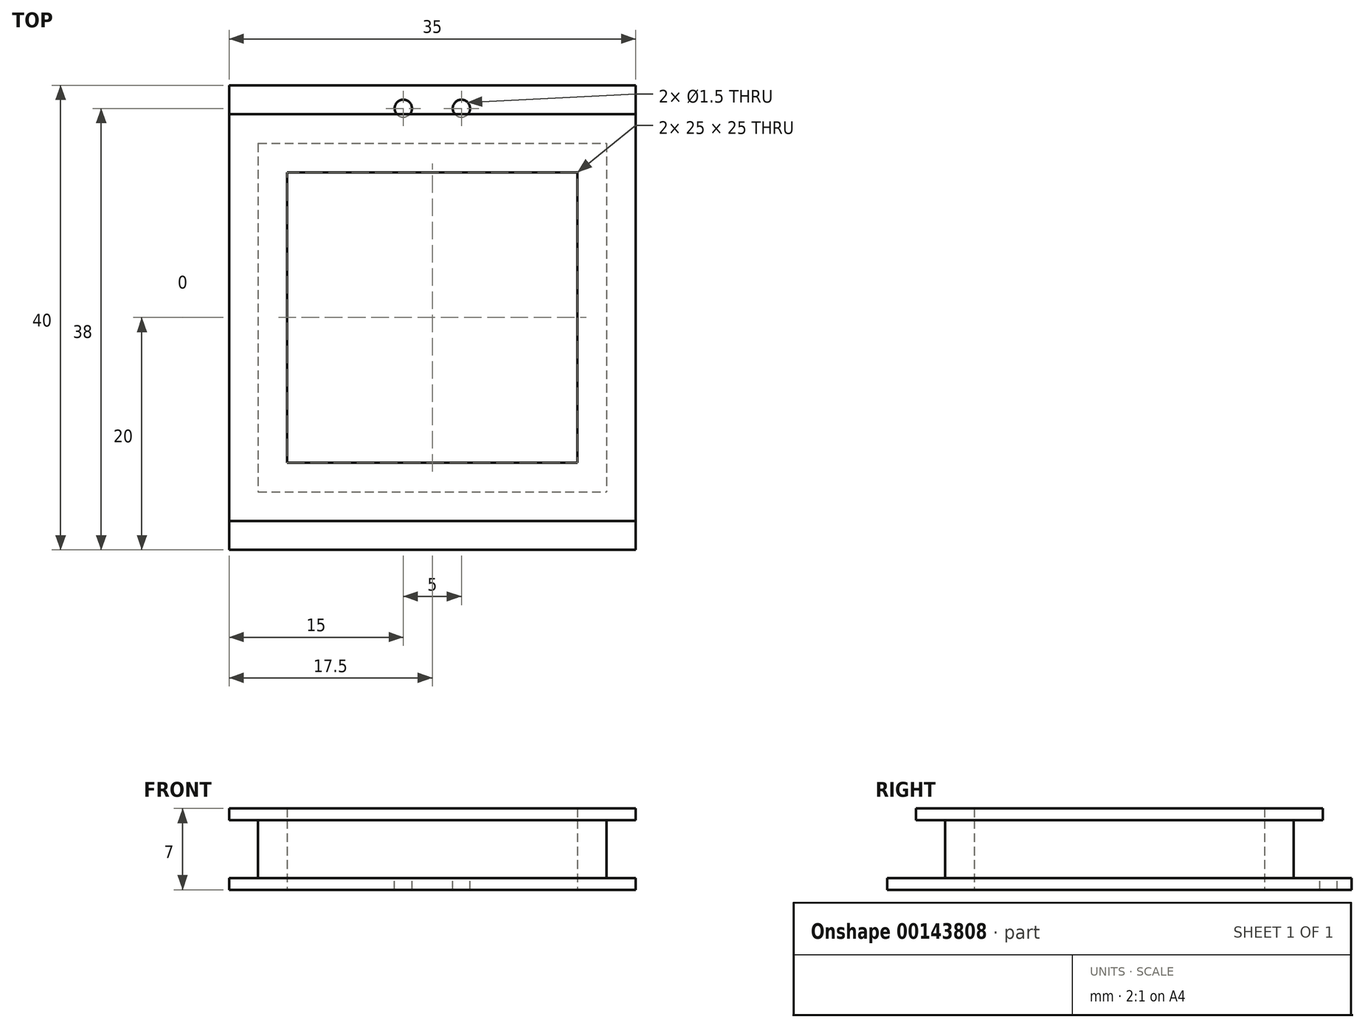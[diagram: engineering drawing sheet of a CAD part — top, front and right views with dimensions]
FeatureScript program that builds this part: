
annotation { "Feature Type Name" : "Feature", "Feature Type Description" : "" }
export const myFeature = defineFeature(function(context is Context, id is Id, definition is map)
    precondition{}
    {
        {
            var Q0;
            Q0=qCreatedBy(makeId("Top.planeOp"),FACE);
            var sketch = newSketch(context, id + "F0", { "sketchPlane" : qUnion([Q0])});
            skLineSegment(sketch, "E0.bottom", {"start": v(-15, 15) * mm, "end": v(15, 15) * mm});
            skLineSegment(sketch, "E0.top", {"start": v(-15, -15) * mm, "end": v(15, -15) * mm});
            skLineSegment(sketch, "E0.left", {"start": v(-15, 15) * mm, "end": v(-15, -15) * mm});
            skLineSegment(sketch, "E0.right", {"start": v(15, 15) * mm, "end": v(15, -15) * mm});
            skPoint(sketch, "E0.middle", {"position": v(0, 0) * mm});
            skLineSegment(sketch, "E1.bottom", {"start": v(-12.5, 12.5) * mm, "end": v(12.5, 12.5) * mm});
            skLineSegment(sketch, "E1.top", {"start": v(-12.5, -12.5) * mm, "end": v(12.5, -12.5) * mm});
            skLineSegment(sketch, "E1.left", {"start": v(-12.5, 12.5) * mm, "end": v(-12.5, -12.5) * mm});
            skLineSegment(sketch, "E1.right", {"start": v(12.5, 12.5) * mm, "end": v(12.5, -12.5) * mm});
            skSolve(sketch);
        }
        {
            var Q0;
            Q0=makeQuery(id+"F0.imprint","IMPRINT",FACE,{"disambiguationData":[TD([[makeQuery(id+"F0.imprint","IMPRINT",EDGE,{"derivedFrom":sQuery(id+"F0.wireOp",EDGE,"E0.bottom")}),-1.0]])]});
            extrude(context, id + "F1", {"entities" : qUnion([Q0]), "depth" : 5 * mm});
        }
        {
            var Q0;
            Q0=makeQuery(id+"F1.opExtrude","CAP_FACE",FACE,{"disambiguationData":[OSD([sQuery(id+"F0.wireOp",EDGE,"E0.bottom"),sQuery(id+"F0.wireOp",EDGE,"E0.top"),sQuery(id+"F0.wireOp",EDGE,"E0.left"),sQuery(id+"F0.wireOp",EDGE,"E0.right"),sQuery(id+"F0.wireOp",EDGE,"E1.bottom"),sQuery(id+"F0.wireOp",EDGE,"E1.top"),sQuery(id+"F0.wireOp",EDGE,"E1.left"),sQuery(id+"F0.wireOp",EDGE,"E1.right")])],"isStart":false});
            var sketch = newSketch(context, id + "F2", { "sketchPlane" : qUnion([Q0])});
            skLineSegment(sketch, "E2.bottom", {"start": v(-17.5, 17.5) * mm, "end": v(17.5, 17.5) * mm});
            skLineSegment(sketch, "E2.top", {"start": v(-17.5, -17.5) * mm, "end": v(17.5, -17.5) * mm});
            skLineSegment(sketch, "E2.left", {"start": v(-17.5, 17.5) * mm, "end": v(-17.5, -17.5) * mm});
            skLineSegment(sketch, "E2.right", {"start": v(17.5, 17.5) * mm, "end": v(17.5, -17.5) * mm});
            skPoint(sketch, "E2.middle", {"position": v(0, 0) * mm});
            skSolve(sketch);
        }
        {
            var Q0;
            Q0=makeQuery(id+"F2.imprint","IMPRINT",FACE,{"disambiguationData":[TD([[makeQuery(id+"F2.imprint","IMPRINT",EDGE,{"derivedFrom":sQuery(id+"F2.wireOp",EDGE,"E2.bottom")}),-1.0]])]});
            var Q1;
            Q1=makeQuery(id+"F2.imprint","IMPRINT",FACE,{"disambiguationData":[TD([[makeQuery(id+"F2.imprint","IMPRINT",EDGE,{"derivedFrom":makeQuery(id+"F1.opExtrude","CAP_EDGE",EDGE,{"disambiguationData":[OSD([sQuery(id+"F0.wireOp",EDGE,"E0.bottom")])],"isStart":false})}),-1.0]])]});
            extrude(context, id + "F3", {"entities" : qUnion([Q0, Q1]), "depth" : 1 * mm});
        }
        {
            var Q0;
            Q0=makeQuery(id+"F1.opExtrude","CAP_FACE",FACE,{"disambiguationData":[OSD([sQuery(id+"F0.wireOp",EDGE,"E0.bottom"),sQuery(id+"F0.wireOp",EDGE,"E0.top"),sQuery(id+"F0.wireOp",EDGE,"E0.left"),sQuery(id+"F0.wireOp",EDGE,"E0.right"),sQuery(id+"F0.wireOp",EDGE,"E1.bottom"),sQuery(id+"F0.wireOp",EDGE,"E1.top"),sQuery(id+"F0.wireOp",EDGE,"E1.left"),sQuery(id+"F0.wireOp",EDGE,"E1.right")])],"isStart":true});
            var sketch = newSketch(context, id + "F4", { "sketchPlane" : qUnion([Q0])});
            skLineSegment(sketch, "E3.bottom", {"start": v(-17.5, 20) * mm, "end": v(17.5, 20) * mm});
            skLineSegment(sketch, "E3.top", {"start": v(-17.5, -20) * mm, "end": v(17.5, -20) * mm});
            skLineSegment(sketch, "E3.left", {"start": v(-17.5, 20) * mm, "end": v(-17.5, -20) * mm});
            skLineSegment(sketch, "E3.right", {"start": v(17.5, 20) * mm, "end": v(17.5, -20) * mm});
            skPoint(sketch, "E3.middle", {"position": v(0, 0) * mm});
            skSolve(sketch);
        }
        {
            var Q0;
            Q0=makeQuery(id+"F4.imprint","IMPRINT",FACE,{"disambiguationData":[TD([[makeQuery(id+"F4.imprint","IMPRINT",EDGE,{"derivedFrom":sQuery(id+"F4.wireOp",EDGE,"E3.bottom")}),-1.0]])]});
            var Q1;
            Q1=makeQuery(id+"F4.imprint","IMPRINT",FACE,{"disambiguationData":[TD([[makeQuery(id+"F4.imprint","IMPRINT",EDGE,{"derivedFrom":makeQuery(id+"F1.opExtrude","CAP_EDGE",EDGE,{"disambiguationData":[OSD([sQuery(id+"F0.wireOp",EDGE,"E0.bottom")])],"isStart":true})}),1.0]])]});
            extrude(context, id + "F5", {"entities" : qUnion([Q0, Q1]), "operationType" : NewBodyOperationType.ADD, "depth" : 1 * mm});
        }
        {
            var Q0;
            Q0=makeQuery(id+"F5.opExtrude","CAP_FACE",FACE,{"disambiguationData":[OSD([sQuery(id+"F0.wireOp",EDGE,"E1.bottom"),sQuery(id+"F0.wireOp",EDGE,"E1.top"),sQuery(id+"F0.wireOp",EDGE,"E1.left"),sQuery(id+"F0.wireOp",EDGE,"E1.right"),sQuery(id+"F4.wireOp",EDGE,"E3.bottom"),sQuery(id+"F4.wireOp",EDGE,"E3.top"),sQuery(id+"F4.wireOp",EDGE,"E3.left"),sQuery(id+"F4.wireOp",EDGE,"E3.right")])],"isStart":true});
            var sketch = newSketch(context, id + "F6", { "sketchPlane" : qUnion([Q0])});
            skCircle(sketch, "E4", {"center": v(-2.5, 18) * mm, "radius": 0.75 * mm});
            skCircle(sketch, "E5", {"center": v(2.5, 18) * mm, "radius": 0.75 * mm});
            skSolve(sketch);
        }
        {
            var Q0;
            Q0=makeQuery(id+"F6.imprint","IMPRINT",FACE,{"disambiguationData":[TD([[makeQuery(id+"F6.imprint","IMPRINT",EDGE,{"derivedFrom":sQuery(id+"F6.wireOp",EDGE,"E4")}),1.0]])]});
            var Q1;
            Q1=makeQuery(id+"F6.imprint","IMPRINT",FACE,{"disambiguationData":[TD([[makeQuery(id+"F6.imprint","IMPRINT",EDGE,{"derivedFrom":sQuery(id+"F6.wireOp",EDGE,"E5")}),1.0]])]});
            extrude(context, id + "F7", {"entities" : qUnion([Q0, Q1]), "operationType" : NewBodyOperationType.REMOVE, "endBound" : BoundingType.THROUGH_ALL, "oppositeDirection" : true, "depth" : 25 * mm});
        }
    });
